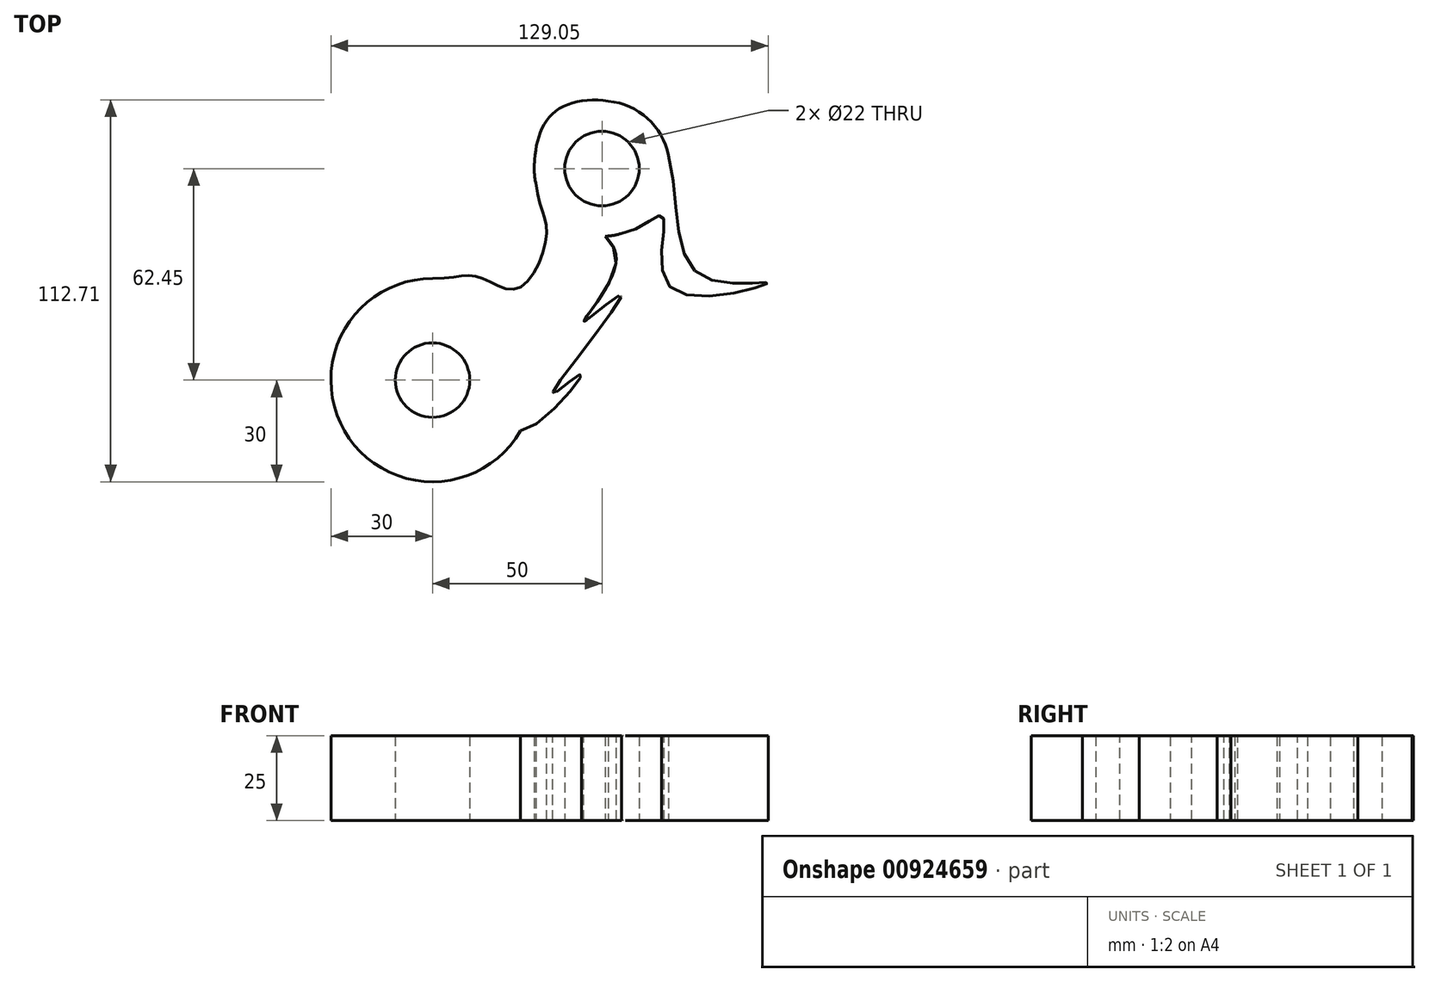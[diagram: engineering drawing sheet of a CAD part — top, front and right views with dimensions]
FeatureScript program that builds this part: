
annotation { "Feature Type Name" : "Feature", "Feature Type Description" : "" }
export const myFeature = defineFeature(function(context is Context, id is Id, definition is map)
    precondition{}
    {
        {
            var Q0;
            Q0=qCreatedBy(makeId("Top.planeOp"),FACE);
            var sketch = newSketch(context, id + "F0", { "sketchPlane" : qUnion([Q0])});
            skCircle(sketch, "E0", {"center": v(0, 0) * mm, "radius": 11 * mm});
            skLineSegment(sketch, "E1", {"start": v(0, 0) * mm, "end": v(0, 100) * mm, "construction": true});
            skLineSegment(sketch, "E2.1.0", {"start": v(0, 0) * mm, "end": v(-86.6, -50) * mm, "construction": true});
            skLineSegment(sketch, "E2.2.0", {"start": v(0, 0) * mm, "end": v(86.6, -50) * mm, "construction": true});
            skCircle(sketch, "E3", {"center": v(50, 62.45) * mm, "radius": 11 * mm});
            skCircle(sketch, "E4", {"center": v(0, 0) * mm, "radius": 30 * mm});
            skFitSpline(sketch, "E5", {"points": [v(0, 30) * mm, v(13.51, 30.47) * mm, v(25.02, 27.04) * mm, v(33.6, 42.6) * mm, v(31.14, 54.4) * mm, v(35.88, 79.02) * mm, v(66.5, 73.66) * mm, v(78.55, 31.32) * mm, v(99.03, 28.7) * mm, v(70.46, 27.2) * mm, v(68, 48.34) * mm, v(56.63, 43.4) * mm, v(48.91, 44.27) * mm, v(54.2, 35.7) * mm, v(44.76, 17.4) * mm, v(55.7, 25) * mm, v(35.51, -3.86) * mm, v(43.85, 1.8) * mm, v(25.98, -15) * mm], "startDerivative": vector(434.02, 0) * mm, "endDerivative": vector(-292.16, -25.9) * mm});
            skCircle(sketch, "E6", {"center": v(50, 62.45) * mm, "radius": 20 * mm});
            skSolve(sketch);
        }
        {
            var Q0;
            Q0 = qSketchRegion(id + "F0", true);
            extrude(context, id + "F1", {"entities" : qUnion([Q0]), "depth" : 25 * mm, "offsetDistance" : 25 * mm});
        }
    });
